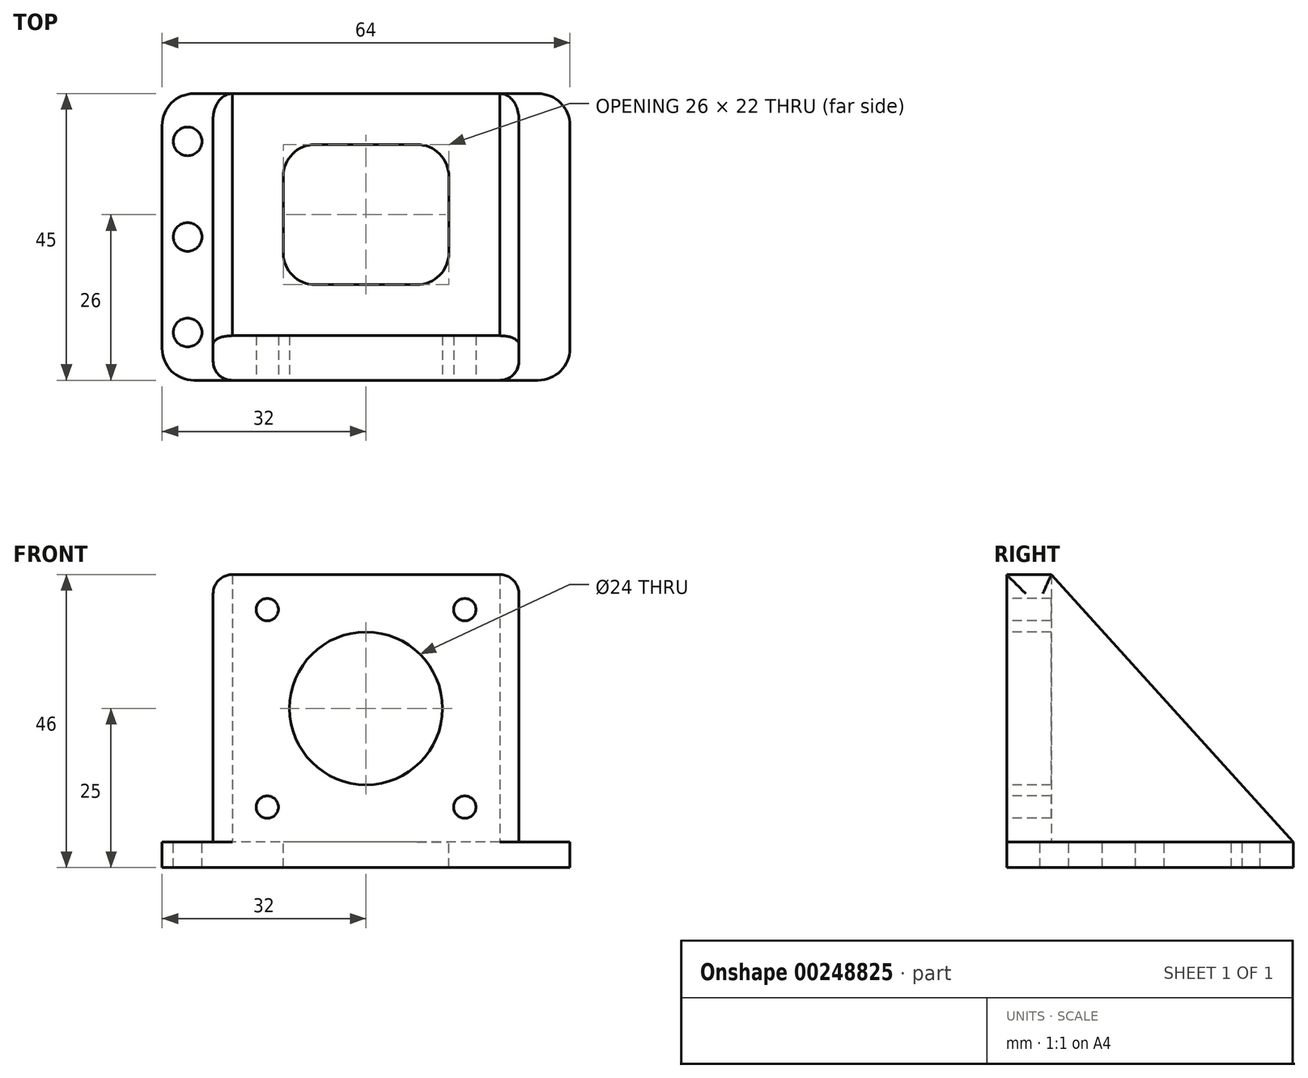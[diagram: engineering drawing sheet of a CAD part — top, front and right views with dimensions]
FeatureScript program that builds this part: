
annotation { "Feature Type Name" : "Feature", "Feature Type Description" : "" }
export const myFeature = defineFeature(function(context is Context, id is Id, definition is map)
    precondition{}
    {
        {
            var Q0;
            Q0=qCreatedBy(makeId("Front.planeOp"),FACE);
            var sketch = newSketch(context, id + "F0", { "sketchPlane" : qUnion([Q0])});
            skCircle(sketch, "E0", {"center": v(0, 0) * mm, "radius": 12 * mm});
            skCircle(sketch, "E1", {"center": v(-15.5, 15.5) * mm, "radius": 1.75 * mm});
            skCircle(sketch, "E2.1.0", {"center": v(-15.5, -15.5) * mm, "radius": 1.75 * mm});
            skCircle(sketch, "E2.2.0", {"center": v(15.5, -15.5) * mm, "radius": 1.75 * mm});
            skCircle(sketch, "E2.3.0", {"center": v(15.5, 15.5) * mm, "radius": 1.75 * mm});
            skLineSegment(sketch, "E3.bottom", {"start": v(21, 21) * mm, "end": v(-21, 21) * mm});
            skLineSegment(sketch, "E3.top", {"start": v(21, -21) * mm, "end": v(-21, -21) * mm});
            skLineSegment(sketch, "E3.left", {"start": v(21, 21) * mm, "end": v(21, -21) * mm});
            skLineSegment(sketch, "E3.right", {"start": v(-21, 21) * mm, "end": v(-21, -21) * mm});
            skLineSegment(sketch, "E4", {"start": v(-21, -21) * mm, "end": v(-32, -21) * mm});
            skLineSegment(sketch, "E5", {"start": v(-32, -21) * mm, "end": v(-32, -25) * mm});
            skLineSegment(sketch, "E6.MirrorCS", {"start": v(32, -21) * mm, "end": v(32, -25) * mm});
            skLineSegment(sketch, "E7.MirrorCS", {"start": v(21, -21) * mm, "end": v(32, -21) * mm});
            skLineSegment(sketch, "E8", {"start": v(32, -25) * mm, "end": v(-32, -25) * mm});
            skLineSegment(sketch, "E9", {"start": v(-24, -21) * mm, "end": v(-24, 21) * mm});
            skLineSegment(sketch, "E10", {"start": v(-21, 21) * mm, "end": v(-24, 21) * mm});
            skLineSegment(sketch, "E11.MirrorCS", {"start": v(24, -21) * mm, "end": v(24, 21) * mm});
            skLineSegment(sketch, "E12.MirrorCS", {"start": v(21, 21) * mm, "end": v(24, 21) * mm});
            skSolve(sketch);
        }
        {
            var Q0;
            Q0=makeQuery(id+"F0.imprint","IMPRINT",FACE,{"disambiguationData":[TD([[makeQuery(id+"F0.imprint","IMPRINT",EDGE,{"derivedFrom":sQuery(id+"F0.wireOp",EDGE,"E0")}),-1.0]])]});
            extrude(context, id + "F1", {"entities" : qUnion([Q0]), "oppositeDirection" : true, "depth" : 7 * mm, "offsetDistance" : 25 * mm});
        }
        {
            var Q0;
            {var subQ0=sQuery(id+"F0.wireOp",EDGE,"E3.left");Q0=makeQuery(id+"F0.imprint","IMPRINT",FACE,{"disambiguationData":[TD([[makeQuery(id+"F0.imprint","IMPRINT",EDGE,{"derivedFrom":subQ0}),1.0]])]});}
            var Q1;
            {var subQ0=sQuery(id+"F0.wireOp",EDGE,"E3.right");Q1=makeQuery(id+"F0.imprint","IMPRINT",FACE,{"disambiguationData":[TD([[makeQuery(id+"F0.imprint","IMPRINT",EDGE,{"derivedFrom":subQ0}),-1.0]])]});}
            extrude(context, id + "F2", {"entities" : qUnion([Q0, Q1]), "operationType" : NewBodyOperationType.ADD, "oppositeDirection" : true, "depth" : (7 + 38) * mm, "offsetDistance" : 25 * mm});
        }
        {
            var Q0;
            {var subQ3=sQuery(id+"F0.wireOp",EDGE,"E3.top");Q0=makeQuery(id+"F0.imprint","IMPRINT",FACE,{"disambiguationData":[TD([[makeQuery(id+"F0.imprint","IMPRINT",EDGE,{"derivedFrom":subQ3}),1.0]])]});}
            var Q1;
            Q1=makeQuery(id+"F2.opExtrude","CAP_FACE",FACE,{"disambiguationData":[OSD([sQuery(id+"F0.wireOp",EDGE,"E3.left"),sQuery(id+"F0.wireOp",EDGE,"E7.MirrorCS"),sQuery(id+"F0.wireOp",EDGE,"E11.MirrorCS"),sQuery(id+"F0.wireOp",EDGE,"E12.MirrorCS")])],"isStart":false});
            extrude(context, id + "F3", {"entities" : qUnion([Q0]), "operationType" : NewBodyOperationType.ADD, "endBound" : BoundingType.UP_TO_SURFACE, "oppositeDirection" : true, "depth" : 25 * mm, "endBoundEntityFace" : qUnion([Q1]), "offsetDistance" : 25 * mm});
        }
        {
            var Q0;
            Q0=makeQuery(id+"F2.opExtrude","CAP_EDGE",EDGE,{"disambiguationData":[OSD([sQuery(id+"F0.wireOp",EDGE,"E12.MirrorCS")])],"isStart":false});
            var Q1;
            Q1=makeQuery(id+"F2.opExtrude","CAP_EDGE",EDGE,{"disambiguationData":[OSD([sQuery(id+"F0.wireOp",EDGE,"E10")])],"isStart":false});
            chamfer(context, id + "F4", {"entities" : qUnion([Q0, Q1]), "chamferType" : ChamferType.TWO_OFFSETS, "width1" : 42 * mm, "oppositeDirection" : false, "width2" : 38 * mm, "tangentPropagation" : true});
        }
        {
            var Q0;
            {var subQ1=sQuery(id+"F0.wireOp",EDGE,"E9");var subQ2=sQuery(id+"F0.wireOp",EDGE,"E4");var subQ6=sQuery(id+"F0.wireOp",EDGE,"E7.MirrorCS");var subQ8=sQuery(id+"F0.wireOp",EDGE,"E3.top");Q0=makeQuery(id+"F3.boolean.opBoolean","SPLIT",FACE,{"disambiguationData":[TD([makeQuery(id+"F2.opExtrude","SWEPT_FACE",FACE,{"disambiguationData":[OSD([subQ1])]})])],"derivedFrom":makeQuery(id+"F3.opExtrude","SWEPT_FACE",FACE,{"disambiguationData":[OSD([subQ8,subQ2,subQ6])]})});}
            var sketch = newSketch(context, id + "F5", { "sketchPlane" : qUnion([Q0])});
            skCircle(sketch, "E13", {"center": v(-28, 22.5) * mm, "radius": 2.25 * mm});
            skPoint(sketch, "E13.centerSnap0", {"position": v(-32, 22.5) * mm});
            skPoint(sketch, "E13.centerSnap1", {"position": v(-28, 0) * mm});
            skCircle(sketch, "E14", {"center": v(-28, 7.5) * mm, "radius": 2.25 * mm});
            skCircle(sketch, "E15", {"center": v(-28, 37.5) * mm, "radius": 2.25 * mm});
            skCircle(sketch, "E16.MirrorC", {"center": v(28, 37.5) * mm, "radius": 2.25 * mm});
            skCircle(sketch, "E17.MirrorC", {"center": v(28, 22.5) * mm, "radius": 2.25 * mm});
            skCircle(sketch, "E18.MirrorC", {"center": v(28, 7.5) * mm, "radius": 2.25 * mm});
            skSolve(sketch);
        }
        {
            var Q0;
            Q0=makeQuery(id+"F5.imprint","IMPRINT",FACE,{"disambiguationData":[TD([[makeQuery(id+"F5.imprint","IMPRINT",EDGE,{"derivedFrom":sQuery(id+"F5.wireOp",EDGE,"E18.MirrorC")}),-1.0]])]});
            var Q1;
            Q1=makeQuery(id+"F5.imprint","IMPRINT",FACE,{"disambiguationData":[TD([[makeQuery(id+"F5.imprint","IMPRINT",EDGE,{"derivedFrom":sQuery(id+"F5.wireOp",EDGE,"E17.MirrorC")}),-1.0]])]});
            var Q2;
            Q2=makeQuery(id+"F5.imprint","IMPRINT",FACE,{"disambiguationData":[TD([[makeQuery(id+"F5.imprint","IMPRINT",EDGE,{"derivedFrom":sQuery(id+"F5.wireOp",EDGE,"E16.MirrorC")}),-1.0]])]});
            var Q3;
            Q3=makeQuery(id+"F5.imprint","IMPRINT",FACE,{"disambiguationData":[TD([[makeQuery(id+"F5.imprint","IMPRINT",EDGE,{"derivedFrom":sQuery(id+"F5.wireOp",EDGE,"E14")}),1.0]])]});
            var Q4;
            Q4=makeQuery(id+"F5.imprint","IMPRINT",FACE,{"disambiguationData":[TD([[makeQuery(id+"F5.imprint","IMPRINT",EDGE,{"derivedFrom":sQuery(id+"F5.wireOp",EDGE,"E13")}),1.0]])]});
            var Q5;
            Q5=makeQuery(id+"F5.imprint","IMPRINT",FACE,{"disambiguationData":[TD([[makeQuery(id+"F5.imprint","IMPRINT",EDGE,{"derivedFrom":sQuery(id+"F5.wireOp",EDGE,"E15")}),1.0]])]});
            extrude(context, id + "F6", {"entities" : qUnion([Q0, Q1, Q2, Q3, Q4, Q5]), "operationType" : NewBodyOperationType.REMOVE, "oppositeDirection" : true, "depth" : 25 * mm, "offsetDistance" : 25 * mm});
        }
        {
            var Q0;
            Q0=makeQuery(id+"F3.opExtrude","CAP_EDGE",EDGE,{"disambiguationData":[OSD([sQuery(id+"F0.wireOp",EDGE,"E5")])],"isStart":true});
            var Q1;
            Q1=makeQuery(id+"F3.opExtrude","CAP_EDGE",EDGE,{"disambiguationData":[OSD([sQuery(id+"F0.wireOp",EDGE,"E5")])],"isStart":false});
            var Q2;
            Q2=makeQuery(id+"F3.opExtrude","CAP_EDGE",EDGE,{"disambiguationData":[OSD([sQuery(id+"F0.wireOp",EDGE,"E6.MirrorCS")])],"isStart":true});
            var Q3;
            Q3=makeQuery(id+"F3.opExtrude","CAP_EDGE",EDGE,{"disambiguationData":[OSD([sQuery(id+"F0.wireOp",EDGE,"E6.MirrorCS")])],"isStart":false});
            fillet(context, id + "F7", {"entities" : qUnion([Q0, Q1, Q2, Q3]), "radius" : 5 * mm, "tangentPropagation" : true, "allowEdgeOverflow" : false});
        }
        {
            var Q0;
            Q0=makeQuery(id+"F2.opExtrude","CAP_EDGE",EDGE,{"disambiguationData":[OSD([sQuery(id+"F0.wireOp",EDGE,"E11.MirrorCS")])],"isStart":true});
            var Q1;
            Q1=makeQuery(id+"F2.opExtrude","CAP_EDGE",EDGE,{"disambiguationData":[OSD([sQuery(id+"F0.wireOp",EDGE,"E9")])],"isStart":true});
            var Q2;
            Q2=makeQuery(id+"F4.opChamfer","BLEND_EDGE",EDGE,{"blendedFrom":[makeQuery(id+"F2.opExtrude","CAP_EDGE",EDGE,{"disambiguationData":[OSD([sQuery(id+"F0.wireOp",EDGE,"E10")])],"isStart":false}),makeQuery(id+"F2.opExtrude","SWEPT_FACE",FACE,{"disambiguationData":[OSD([sQuery(id+"F0.wireOp",EDGE,"E9")])]})],"blendedInto":[makeQuery(id+"F2.opExtrude","SWEPT_FACE",FACE,{"disambiguationData":[OSD([sQuery(id+"F0.wireOp",EDGE,"E9")])]})]});
            var Q3;
            Q3=makeQuery(id+"F2.opExtrude","SWEPT_EDGE",EDGE,{"disambiguationData":[OSD([sQuery(id+"F0.wireOp",EDGE,"E9"),sQuery(id+"F0.wireOp",EDGE,"E10")])]});
            var Q4;
            Q4=makeQuery(id+"F2.opExtrude","SWEPT_EDGE",EDGE,{"disambiguationData":[OSD([sQuery(id+"F0.wireOp",EDGE,"E11.MirrorCS"),sQuery(id+"F0.wireOp",EDGE,"E12.MirrorCS")])]});
            var Q5;
            Q5=makeQuery(id+"F4.opChamfer","BLEND_EDGE",EDGE,{"blendedFrom":[makeQuery(id+"F2.opExtrude","CAP_EDGE",EDGE,{"disambiguationData":[OSD([sQuery(id+"F0.wireOp",EDGE,"E12.MirrorCS")])],"isStart":false}),makeQuery(id+"F2.opExtrude","SWEPT_FACE",FACE,{"disambiguationData":[OSD([sQuery(id+"F0.wireOp",EDGE,"E11.MirrorCS")])]})],"blendedInto":[makeQuery(id+"F2.opExtrude","SWEPT_FACE",FACE,{"disambiguationData":[OSD([sQuery(id+"F0.wireOp",EDGE,"E11.MirrorCS")])]})]});
            fillet(context, id + "F8", {"entities" : qUnion([Q0, Q1, Q2, Q3, Q4, Q5]), "radius" : 3 * mm, "tangentPropagation" : true, "allowEdgeOverflow" : false});
        }
        {
            var Q0;
            {var subQ1=sQuery(id+"F0.wireOp",EDGE,"E7.MirrorCS");var subQ2=sQuery(id+"F0.wireOp",EDGE,"E3.left");var subQ3=sQuery(id+"F0.wireOp",EDGE,"E3.top");var subQ4=sQuery(id+"F0.wireOp",EDGE,"E4");Q0=makeQuery(id+"F3.boolean.opBoolean","SPLIT",FACE,{"disambiguationData":[TD([makeQuery(id+"F2.opExtrude","SWEPT_FACE",FACE,{"disambiguationData":[OSD([subQ2])]})])],"derivedFrom":makeQuery(id+"F3.opExtrude","SWEPT_FACE",FACE,{"disambiguationData":[OSD([subQ3,subQ4,subQ1])]})});}
            var sketch = newSketch(context, id + "F9", { "sketchPlane" : qUnion([Q0])});
            skLineSegment(sketch, "E19", {"start": v(21, 45) * mm, "end": v(-21, 45) * mm});
            skLineSegment(sketch, "E20", {"start": v(-21, 45) * mm, "end": v(-21, 7) * mm});
            skLineSegment(sketch, "E21", {"start": v(-21, 7) * mm, "end": v(21, 7) * mm});
            skLineSegment(sketch, "E22.0", {"start": v(13, 37) * mm, "end": v(-13, 37) * mm});
            skLineSegment(sketch, "E22.1", {"start": v(13, 15) * mm, "end": v(13, 37) * mm});
            skLineSegment(sketch, "E22.2", {"start": v(-13, 15) * mm, "end": v(13, 15) * mm});
            skLineSegment(sketch, "E22.3", {"start": v(-13, 37) * mm, "end": v(-13, 15) * mm});
            skSolve(sketch);
        }
        {
            var Q0;
            Q0=makeQuery(id+"F9.imprint","IMPRINT",FACE,{"disambiguationData":[TD([[makeQuery(id+"F9.imprint","IMPRINT",EDGE,{"derivedFrom":sQuery(id+"F9.wireOp",EDGE,"E22.0")}),1.0]])]});
            extrude(context, id + "F10", {"entities" : qUnion([Q0]), "operationType" : NewBodyOperationType.REMOVE, "oppositeDirection" : true, "depth" : 25 * mm, "offsetDistance" : 25 * mm});
        }
        {
            var Q0;
            Q0=makeQuery(id+"F10.boolean.opBoolean","COPY",EDGE,{"derivedFrom":makeQuery(id+"F10.opExtrude","SWEPT_EDGE",EDGE,{"disambiguationData":[OSD([sQuery(id+"F9.wireOp",EDGE,"E22.1"),sQuery(id+"F9.wireOp",EDGE,"E22.2")])]})});
            var Q1;
            Q1=makeQuery(id+"F10.boolean.opBoolean","COPY",EDGE,{"derivedFrom":makeQuery(id+"F10.opExtrude","SWEPT_EDGE",EDGE,{"disambiguationData":[OSD([sQuery(id+"F9.wireOp",EDGE,"E22.2"),sQuery(id+"F9.wireOp",EDGE,"E22.3")])]})});
            var Q2;
            Q2=makeQuery(id+"F10.boolean.opBoolean","COPY",EDGE,{"derivedFrom":makeQuery(id+"F10.opExtrude","SWEPT_EDGE",EDGE,{"disambiguationData":[OSD([sQuery(id+"F9.wireOp",EDGE,"E22.0"),sQuery(id+"F9.wireOp",EDGE,"E22.3")])]})});
            var Q3;
            Q3=makeQuery(id+"F10.boolean.opBoolean","COPY",EDGE,{"derivedFrom":makeQuery(id+"F10.opExtrude","SWEPT_EDGE",EDGE,{"disambiguationData":[OSD([sQuery(id+"F9.wireOp",EDGE,"E22.0"),sQuery(id+"F9.wireOp",EDGE,"E22.1")])]})});
            fillet(context, id + "F11", {"entities" : qUnion([Q0, Q1, Q2, Q3]), "radius" : 5 * mm, "tangentPropagation" : true, "allowEdgeOverflow" : false});
        }
    });
